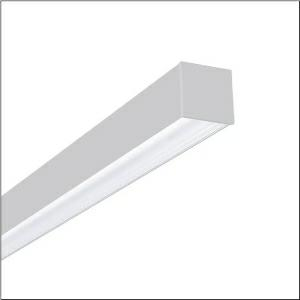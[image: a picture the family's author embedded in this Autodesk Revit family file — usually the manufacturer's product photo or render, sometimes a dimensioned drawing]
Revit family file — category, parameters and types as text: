
# Revit family: silica_r_5mx31bd2w4a_93b3
name_source: partatom
category: Lighting Fixtures
units: mm (PartAtom-declared; Revit-internal decimal feet)

## family parameters
Cut with Voids When Loaded = No
Host = Face
Light Source = No
Part Type = Normal
Room Calculation Point = No
Round Connector Dimension = Use Diameter
Shared = No

## types (1)
- --- (1 x LED, 14160 lm, 92.6 W, 4000K)
    Apparent Load = 93 VA
    CIE Flux Codes = 82 97 100 70 100
    Color Rendering = 80
    Color Temperature = 4000K
    Default Elevation = 1800 mm
    Description = Silica®, office luminaire, of aluminium, light emission: direct/indirect distribution, primary light characteristic: symmetric, installation type: suspended mounting, LED rated luminous flux: 14.160 lm, light colour: 840, colour temperature: 4000K, control gear: ECG DALI, with terminal, 3+2-pole, max. 2.5mm², mains connection: 230V, AC, 50/60Hz, connection cable inclusive, cable length: 1,5 m, rated input power: 93W, luminaire housing, of aluminium, traffic white (RAL 9016), length: 2.844 mm, width: 65 mm, height: 64mm, protection rating (complete): IP20, insulation class (complete): insulation class I (protective earthing), certification: CE, permissible ambient temperature for indoor applications: 0..+35°C, standard: EN 50419, packaging unit: 1 piece
    Height = 64 mm
    Lamp = 1 x LED
    Lamp Light Flux = 14160 lm
    Lamp Power = 92.6 W
    Lamp count = 1
    Length = 2845 mm
    Luminous efficacy = 153 lm/W
    Manufacturer = Siteco
    ModVariant = No
    Model = 5MX31BD2W4A
    Mounting Place = Ceiling
    Mounting Type = Pendant
    Number of Poles = 1
    OnlyDefault = Yes
    Power Factor = 1
    Product Name = Silica®
    Product group = office luminaire | ceiling pendant
    ProductGroupID = 905
    Protection Class = Protection class I
    Protection Degree = IP 20
    RLX_Detail_Level = 1
    RlxData = <blob elided: 28837 chars, md5=d7c73677>
    Socket = socket
    Standby Power = 0 W
    System Light Flux = 14160 lm
    System Power = 93 W
    Type Comments = factory setting: direct and indirect light
    Type Image = l_1003924.jpg
    URL = http://relux.com
    VarID = @adj_131722
    Voltage = 0 V
    Weight = 0.00 kg
    Width = 66 mm

## geometry (parser evidence)
native form markers: Blend x4, Sweep x13
no freeform markers — native parametric forms only
